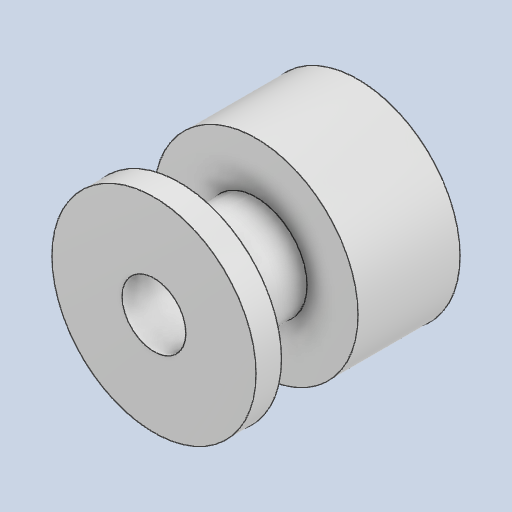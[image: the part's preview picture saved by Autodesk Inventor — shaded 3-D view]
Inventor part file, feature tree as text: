
AUTODESK INVENTOR PART (.ipt)
format: ipt  version: 2024 (Build 280153000, 153)  size: 252,416 bytes
history: native  units: mm
features: extrude x2, sketch x2, plane x1, projected_geometry x1
ambient origin geometry x8: Origin, YZ Plane, XZ Plane, XY Plane, X Axis, Y Axis, Z Axis, Center Point
bodies: Solid1 (feature_tree)
feature tree (6):
  extrude  "Extrusion1"  Depth=16.0mm TaperAngle=0.0deg
  plane  "Work Plane1"
  extrude  "Extrusion2"  [1 undecoded]
  sketch  "Sketch1"  dims[d0=16.0mm d1=16.0mm d2=0.0mm]
  sketch  "Sketch3"  dims[d3=5.0mm d4=-2.0mm d5=5.0mm d6=8.0mm d7=6.0mm d8=0.0mm]
  projected_geometry  "Projected Loop1"
note: 1 required parameter value undecoded (feature->parameter linkage not recoverable at this tier; creation-order binding heuristic only, values carry confidence <= 0.55)
